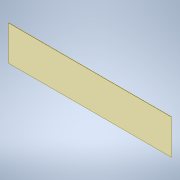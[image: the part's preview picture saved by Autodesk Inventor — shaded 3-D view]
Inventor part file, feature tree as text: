
AUTODESK INVENTOR PART (.ipt)
format: ipt  version: 2021 (Build 250183000, 183)  size: 90,624 bytes
history: native  units: mm
features: extrude x1, sketch x1
ambient origin geometry x8: Origin, YZ Plane, XZ Plane, XY Plane, X Axis, Y Axis, Z Axis, Center Point
bodies: Solid1 (feature_tree)
feature tree (2):
  extrude  "Extrusion1"  Depth=427.0mm
  sketch  "Sketch1"  dims[d0=2000.0mm d1=427.0mm d2=3.0mm d3=0.0mm]
